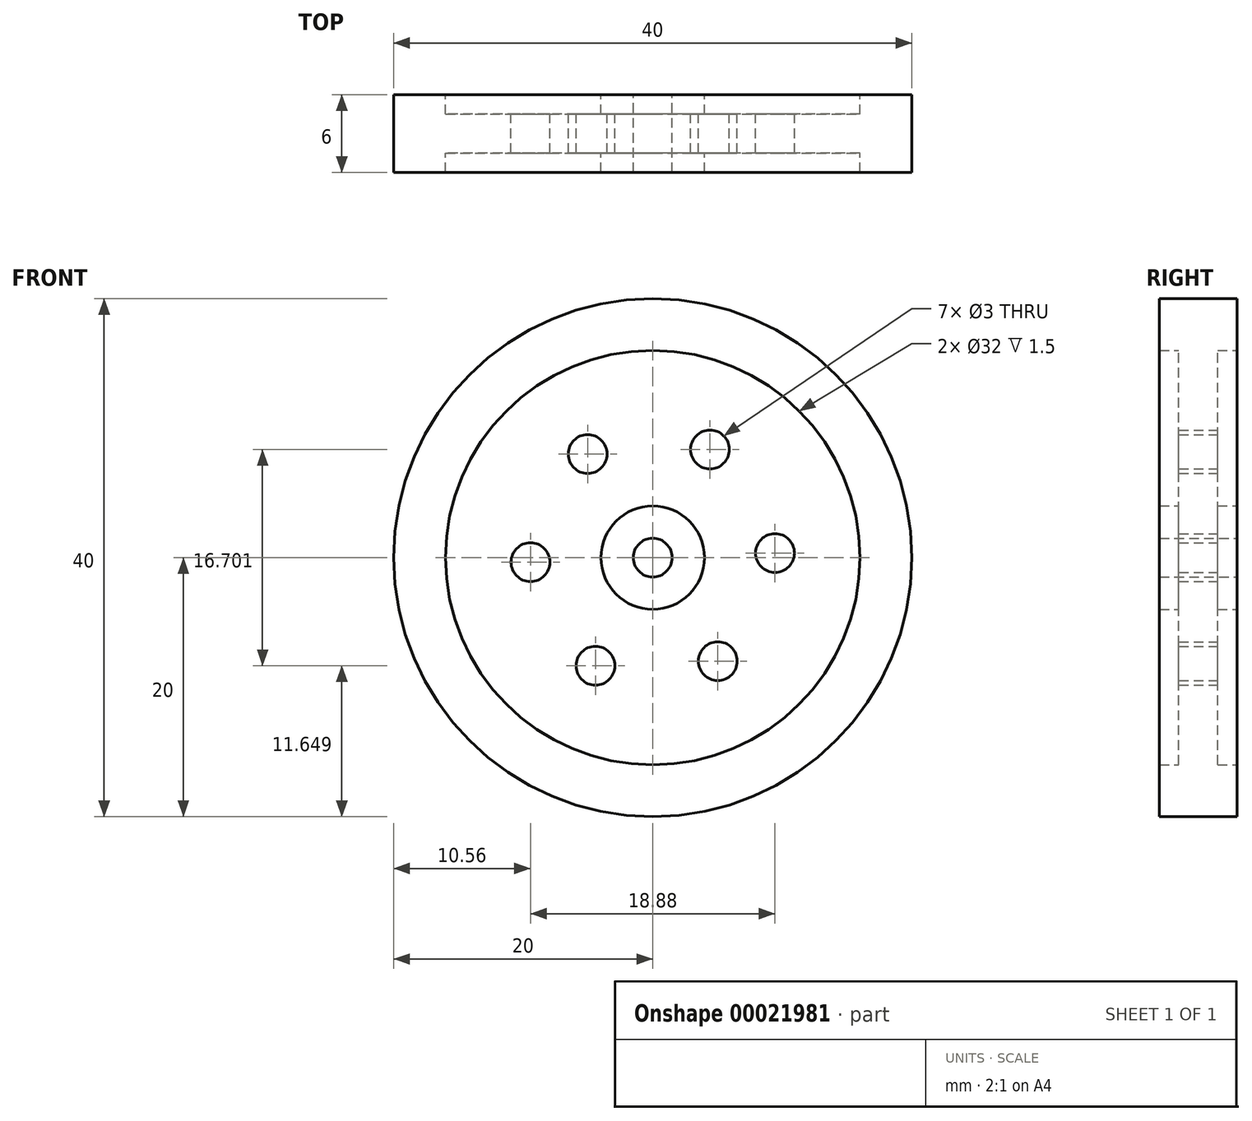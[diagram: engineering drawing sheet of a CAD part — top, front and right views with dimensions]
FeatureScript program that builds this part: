
annotation { "Feature Type Name" : "Feature", "Feature Type Description" : "" }
export const myFeature = defineFeature(function(context is Context, id is Id, definition is map)
    precondition{}
    {
        {
            var Q0;
            Q0=qCreatedBy(makeId("Front.planeOp"),FACE);
            var sketch = newSketch(context, id + "F0", { "sketchPlane" : qUnion([Q0])});
            skCircle(sketch, "E0", {"center": v(0, 0) * mm, "radius": 20 * mm});
            skCircle(sketch, "E1", {"center": v(0, 0) * mm, "radius": 16 * mm});
            skCircle(sketch, "E2", {"center": v(0, 0) * mm, "radius": 4 * mm});
            skCircle(sketch, "E3", {"center": v(-5.02, 8) * mm, "radius": 1.5 * mm});
            skCircle(sketch, "E4.1.0", {"center": v(-9.44, -0.35) * mm, "radius": 1.5 * mm});
            skCircle(sketch, "E4.2.0", {"center": v(-4.42, -8.35) * mm, "radius": 1.5 * mm});
            skCircle(sketch, "E4.3.0", {"center": v(5.02, -8) * mm, "radius": 1.5 * mm});
            skCircle(sketch, "E4.4.0", {"center": v(9.44, 0.35) * mm, "radius": 1.5 * mm});
            skCircle(sketch, "E4.5.0", {"center": v(4.42, 8.35) * mm, "radius": 1.5 * mm});
            skCircle(sketch, "E5", {"center": v(0, 0) * mm, "radius": 1.5 * mm});
            skSolve(sketch);
        }
        {
            var Q0;
            Q0=makeQuery(id+"F0.imprint","IMPRINT",FACE,{"disambiguationData":[TD([[makeQuery(id+"F0.imprint","IMPRINT",EDGE,{"derivedFrom":sQuery(id+"F0.wireOp",EDGE,"E1")}),1.0]])]});
            extrude(context, id + "F1", {"entities" : qUnion([Q0]), "endBound" : BoundingType.SYMMETRIC, "depth" : 3 * mm});
        }
        {
            var Q0;
            Q0=makeQuery(id+"F0.imprint","IMPRINT",FACE,{"disambiguationData":[TD([[makeQuery(id+"F0.imprint","IMPRINT",EDGE,{"derivedFrom":sQuery(id+"F0.wireOp",EDGE,"E2")}),1.0]])]});
            var Q1;
            Q1=makeQuery(id+"F0.imprint","IMPRINT",FACE,{"disambiguationData":[TD([[makeQuery(id+"F0.imprint","IMPRINT",EDGE,{"derivedFrom":sQuery(id+"F0.wireOp",EDGE,"E0")}),1.0]])]});
            extrude(context, id + "F2", {"entities" : qUnion([Q0, Q1]), "operationType" : NewBodyOperationType.ADD, "endBound" : BoundingType.SYMMETRIC, "depth" : 6 * mm});
        }
        {
            var Q0;
            Q0=sQuery(id+"F0.wireOp",VERTEX,"E0.center");
            var Q1;
            Q1=makeQuery(id+"F1.opExtrude","SWEPT_BODY",BODY,{"disambiguationData":[OSD([sQuery(id+"F0.wireOp",EDGE,"E1"),sQuery(id+"F0.wireOp",EDGE,"E2"),sQuery(id+"F0.wireOp",EDGE,"E3"),sQuery(id+"F0.wireOp",EDGE,"E4.1.0"),sQuery(id+"F0.wireOp",EDGE,"E4.2.0"),sQuery(id+"F0.wireOp",EDGE,"E4.3.0"),sQuery(id+"F0.wireOp",EDGE,"E4.4.0"),sQuery(id+"F0.wireOp",EDGE,"E4.5.0")])]});
            hole(context, id + "F3", {"style" : HoleStyle.SIMPLE, "holeDiameter" : 3 * mm, "endStyle" : HoleEndStyle.THROUGH, "locations" : qUnion([Q0]), "scope" : qUnion([Q1])});
        }
    });
